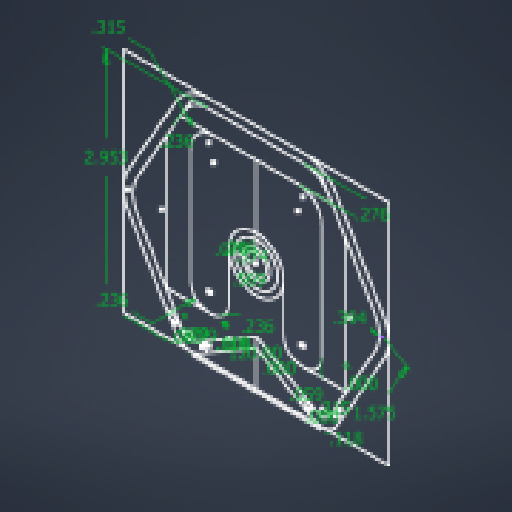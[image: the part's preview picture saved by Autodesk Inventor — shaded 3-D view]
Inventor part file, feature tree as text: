
AUTODESK INVENTOR PART (.ipt)
format: ipt  version: 2023 (Build 270158000, 158)  size: 223,744 bytes
history: native  units: in
note: dims shown in document units (in); Inventor stores cm internally (conversion verified against a paired STEP export)
features: extrude x5, sketch x1
ambient origin geometry x8: Origin, YZ Plane, XZ Plane, XY Plane, X Axis, Y Axis, Z Axis, Center Point
bodies: Solid1 (feature_tree)
feature tree (6):
  sketch  "Sketch1"  dims[d0=0.374in d1=120.0deg d2=2.9528in d3=1.5748in d4=0.1181in d5=0.3937in d6=0.2657in d7=0.1181in d8=0.315in d9=0.2362in d10=0.2362in d11=0.5689in d12=0.0787in d13=0.0787in d14=0.0787in d15=0.2362in d16=0.0in d17=0.0in d18=0.0in d19=0.0in d20=0.0in d21=0.0591in d22=0.2756in d23=0.315in d24=0.1969in d25=0.0in d26=0.1575in d27=0.0in d28=0.0in d29=0.0in d32=0.0138in d33=0.0in d34=0.0039in d35=0.0in]
  extrude  "Extrusion1"  Depth=0.1969in TaperAngle=0.0deg
  extrude  "Extrusion2"  Depth=0.1575in TaperAngle=0.0deg
  extrude  "Extrusion3"  TaperAngle=0.0deg  [1 undecoded]
  extrude  "Extrusion5"  Depth=0.0138in TaperAngle=0.0deg
  extrude  "Extrusion6"  Depth=0.0039in TaperAngle=0.0deg
note: 1 required parameter value undecoded (feature->parameter linkage not recoverable at this tier; creation-order binding heuristic only, values carry confidence <= 0.55)
